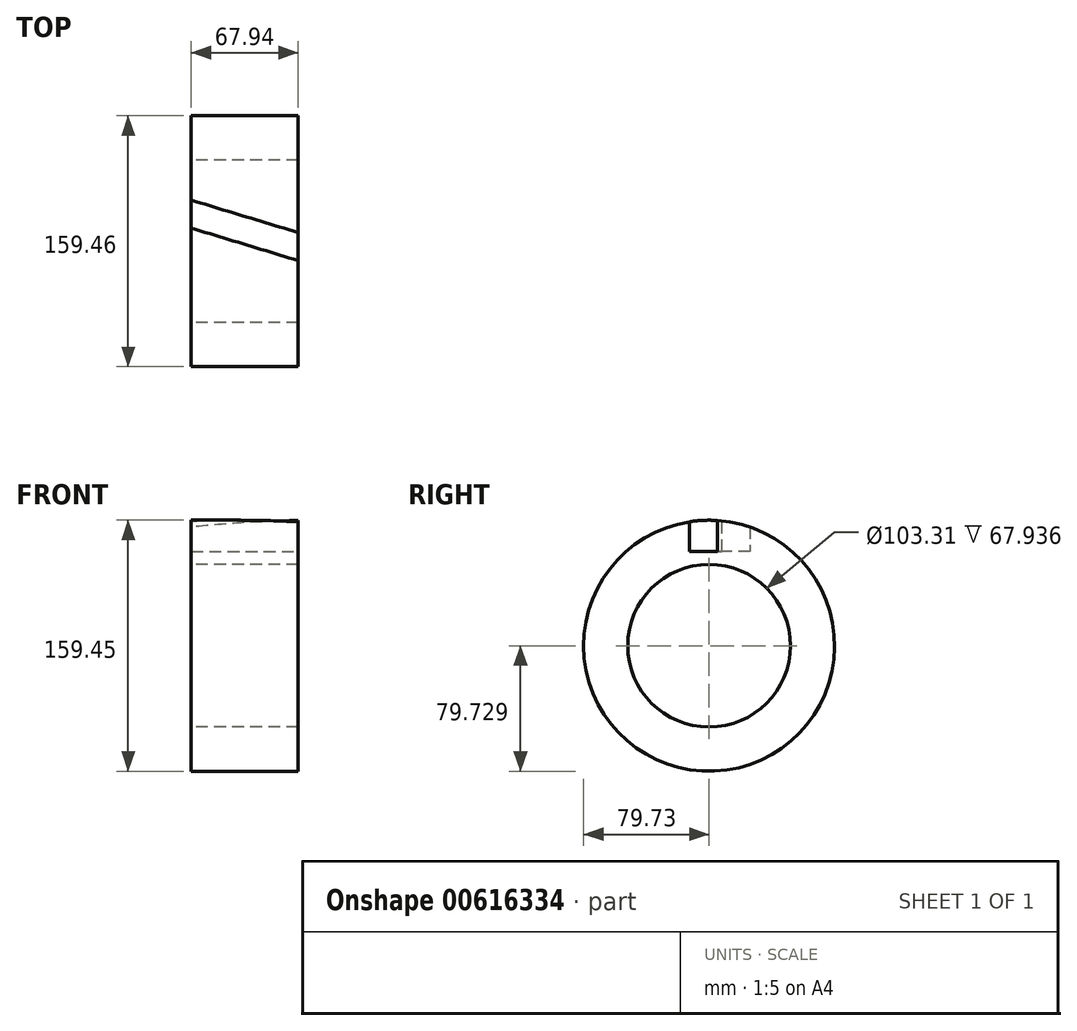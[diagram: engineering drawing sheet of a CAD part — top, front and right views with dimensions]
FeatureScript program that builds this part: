
annotation { "Feature Type Name" : "Feature", "Feature Type Description" : "" }
export const myFeature = defineFeature(function(context is Context, id is Id, definition is map)
    precondition{}
    {
        {
            var Q0;
            Q0=qCreatedBy(makeId("Front.planeOp"),FACE);
            var sketch = newSketch(context, id + "F0", { "sketchPlane" : qUnion([Q0])});
            skLineSegment(sketch, "E0.bottom", {"start": v(-32.55, 52.83) * mm, "end": v(35.39, 52.83) * mm});
            skLineSegment(sketch, "E0.top", {"start": v(-32.55, 24.76) * mm, "end": v(35.39, 24.76) * mm});
            skLineSegment(sketch, "E0.left", {"start": v(-32.55, 52.83) * mm, "end": v(-32.55, 24.76) * mm});
            skLineSegment(sketch, "E0.right", {"start": v(35.39, 52.83) * mm, "end": v(35.39, 24.76) * mm});
            skLineSegment(sketch, "E1", {"start": v(-47.86, -26.9) * mm, "end": v(65, -26.9) * mm});
            skSolve(sketch);
        }
        {
            var Q0;
            Q0 = qSketchRegion(id + "F0", true);
            var Q1;
            Q1=sQuery(id+"F0.wireOp",EDGE,"E1");
            revolve(context, id + "F1", {"entities" : qUnion([Q0]), "axis" : qUnion([Q1]), "revolveType" : RevolveType.FULL});
        }
        {
            var Q0;
            Q0=qCreatedBy(makeId("Top.planeOp"),FACE);
            cPlane(context, id + "F2", {"entities" : qUnion([Q0]), "cplaneType" : CPlaneType.OFFSET, "offset" : 53.96 * mm, "width" : 152.4 * mm, "height" : 152.4 * mm});
        }
        {
            var Q0;
            Q0=qCreatedBy(id+"F2.planeOp",FACE);
            var sketch = newSketch(context, id + "F3", { "sketchPlane" : qUnion([Q0])});
            skLineSegment(sketch, "E2", {"start": v(-46.06, 30.16) * mm, "end": v(53.35, 0) * mm});
            skLineSegment(sketch, "E3", {"start": v(53.35, 0) * mm, "end": v(53.23, -17.8) * mm});
            skLineSegment(sketch, "E4", {"start": v(53.23, -17.8) * mm, "end": v(-45.96, 12.39) * mm});
            skLineSegment(sketch, "E5", {"start": v(-45.96, 12.39) * mm, "end": v(-46.06, 30.16) * mm});
            skSolve(sketch);
        }
        {
            var Q0;
            Q0 = qSketchRegion(id + "F3", true);
            extrude(context, id + "F4", {"entities" : qUnion([Q0]), "operationType" : NewBodyOperationType.REMOVE, "oppositeDirection" : true, "depth" : 20.97 * mm, "offsetDistance" : 25.4 * mm});
        }
    });
